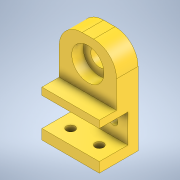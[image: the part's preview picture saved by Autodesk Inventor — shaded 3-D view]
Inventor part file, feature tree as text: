
AUTODESK INVENTOR PART (.ipt)
format: ipt  version: 2020 (Build 240168000, 168)  size: 187,904 bytes
history: native  units: mm
features: extrude x8, sketch x8, fillet x1
ambient origin geometry x8: Origin, YZ Plane, XZ Plane, XY Plane, X Axis, Y Axis, Z Axis, Center Point
bodies: Solid1 (feature_tree)
feature tree (17):
  extrude  "Extrusion1"  Depth=60.0mm
  extrude  "Extrusion2"  Depth=15.0mm
  extrude  "Extrusion3"  Depth=8.0mm TaperAngle=0.0deg
  fillet  "Fillet1"  Radius=12.0mm
  extrude  "Extrusion4"  Depth=16.0mm
  extrude  "Extrusion5"  Depth=8.0mm TaperAngle=0.0deg
  extrude  "Extrusion6"  Depth=7.0mm TaperAngle=0.0deg
  extrude  "Extrusion7"  Depth=6.0mm
  extrude  "Extrusion8"  Depth=20.0mm
  sketch  "Sketch1"  dims[d0=40.0mm d1=60.0mm]
  sketch  "Sketch2"  dims[d2=15.0mm d3=0.0mm d4=22.5mm]
  sketch  "Sketch3"  dims[d5=43.0mm d6=8.0mm d7=0.0mm d8=12.0mm]
  sketch  "Sketch4"  dims[d9=8.0mm d10=0.0mm d11=16.0mm]
  sketch  "Sketch5"  dims[d12=20.0mm d13=8.0mm d14=0.0mm]
  sketch  "Sketch6"  dims[d15=27.0mm d16=7.0mm d17=0.0mm]
  sketch  "Sketch7"  dims[d19=6.0mm d20=6.0mm]
  sketch  "Sketch8"  dims[d21=10.0mm d22=20.0mm d23=10.0mm d24=10.0mm d25=7.0mm d26=0.0mm d27=6.0mm d28=6.0mm d29=10.0mm d30=10.0mm d31=20.0mm d32=10.0mm d33=7.0mm d34=0.0mm d35=5.0mm d36=12.0mm d37=0.0mm]
